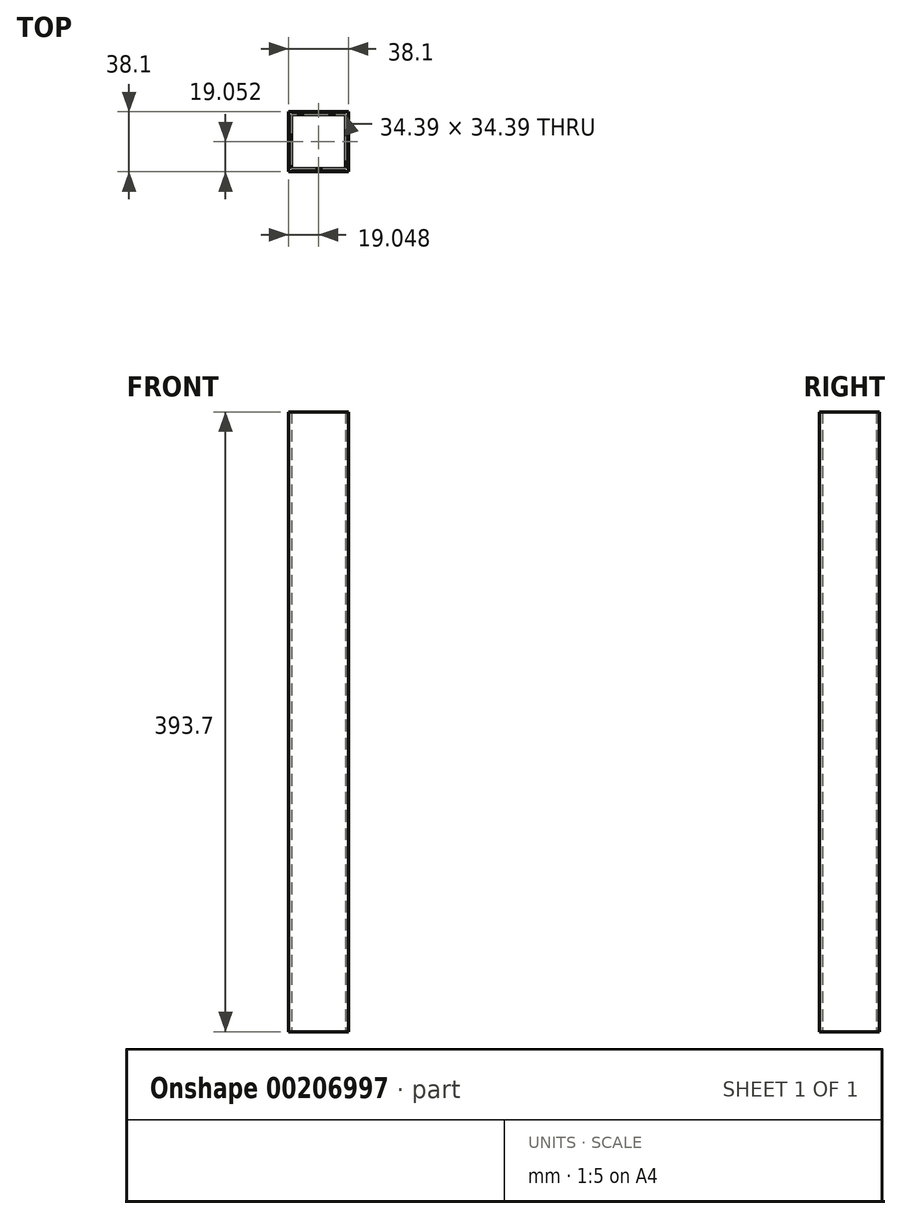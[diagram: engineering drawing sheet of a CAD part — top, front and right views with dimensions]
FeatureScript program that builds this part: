
annotation { "Feature Type Name" : "Feature", "Feature Type Description" : "" }
export const myFeature = defineFeature(function(context is Context, id is Id, definition is map)
    precondition{}
    {
        {
            var Q0;
            Q0=qCreatedBy(makeId("Top.planeOp"),FACE);
            var sketch = newSketch(context, id + "F0", { "sketchPlane" : qUnion([Q0])});
            skLineSegment(sketch, "E0.bottom", {"start": v(-80.1, -65.97) * mm, "end": v(-42, -65.97) * mm});
            skLineSegment(sketch, "E0.top", {"start": v(-80.1, -27.87) * mm, "end": v(-42, -27.87) * mm});
            skLineSegment(sketch, "E0.left", {"start": v(-80.1, -65.97) * mm, "end": v(-80.1, -27.87) * mm});
            skLineSegment(sketch, "E0.right", {"start": v(-42, -65.97) * mm, "end": v(-42, -27.87) * mm});
            skLineSegment(sketch, "E1.bottom", {"start": v(-78.25, -64.11) * mm, "end": v(-43.86, -64.11) * mm});
            skLineSegment(sketch, "E1.top", {"start": v(-78.25, -29.72) * mm, "end": v(-43.86, -29.72) * mm});
            skLineSegment(sketch, "E1.left", {"start": v(-78.25, -64.11) * mm, "end": v(-78.25, -29.72) * mm});
            skLineSegment(sketch, "E1.right", {"start": v(-43.86, -64.11) * mm, "end": v(-43.86, -29.72) * mm});
            skSolve(sketch);
        }
        {
            var Q0;
            Q0 = qSketchRegion(id + "F0", true);
            extrude(context, id + "F1", {"entities" : qUnion([Q0]), "depth" : 393.7 * mm});
        }
    });
